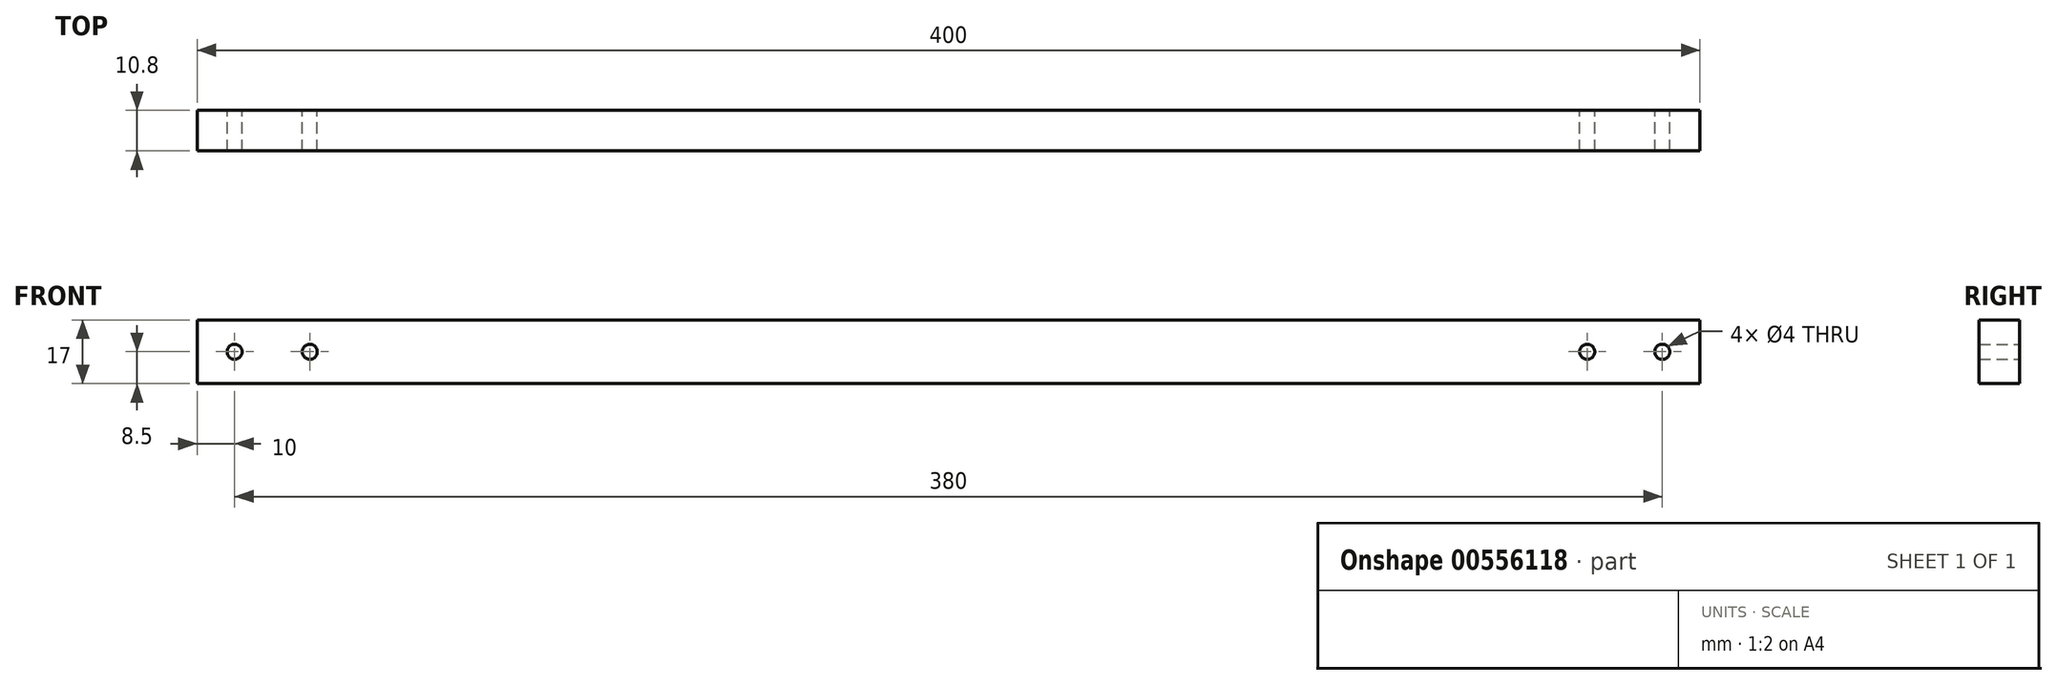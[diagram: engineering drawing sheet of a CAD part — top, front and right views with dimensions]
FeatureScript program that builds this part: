
annotation { "Feature Type Name" : "Feature", "Feature Type Description" : "" }
export const myFeature = defineFeature(function(context is Context, id is Id, definition is map)
    precondition{}
    {
        {
            var Q0;
            Q0=qCreatedBy(makeId("Front.planeOp"),FACE);
            var sketch = newSketch(context, id + "F0", { "sketchPlane" : qUnion([Q0])});
            skLineSegment(sketch, "E0.bottom", {"start": v(200, 8.5) * mm, "end": v(-200, 8.5) * mm});
            skLineSegment(sketch, "E0.top", {"start": v(200, -8.5) * mm, "end": v(-200, -8.5) * mm});
            skLineSegment(sketch, "E0.left", {"start": v(200, 8.5) * mm, "end": v(200, -8.5) * mm});
            skLineSegment(sketch, "E0.right", {"start": v(-200, 8.5) * mm, "end": v(-200, -8.5) * mm});
            skPoint(sketch, "E0.middle", {"position": v(0, 0) * mm});
            skLineSegment(sketch, "E1", {"start": v(-200, 0) * mm, "end": v(200, 0) * mm, "construction": true});
            skPoint(sketch, "E2", {"position": v(-190, 0) * mm});
            skPoint(sketch, "E3", {"position": v(-170, 0) * mm});
            skPoint(sketch, "E4", {"position": v(190, 0) * mm});
            skPoint(sketch, "E5", {"position": v(170, 0) * mm});
            skSolve(sketch);
        }
        {
            var Q0;
            Q0 = qSketchRegion(id + "F0", true);
            extrude(context, id + "F1", {"entities" : qUnion([Q0]), "depth" : 10.8 * mm, "offsetDistance" : 25 * mm});
        }
        {
            var Q0;
            Q0=sQuery(id+"F0.wireOp",VERTEX,"E2");
            var Q1;
            Q1=sQuery(id+"F0.wireOp",VERTEX,"E3");
            var Q2;
            Q2=sQuery(id+"F0.wireOp",VERTEX,"E5");
            var Q3;
            Q3=sQuery(id+"F0.wireOp",VERTEX,"E4");
            var Q4;
            Q4=makeQuery(id+"F1.opExtrude","SWEPT_BODY",BODY,{"disambiguationData":[OSD([sQuery(id+"F0.wireOp",EDGE,"E0.bottom"),sQuery(id+"F0.wireOp",EDGE,"E0.top"),sQuery(id+"F0.wireOp",EDGE,"E0.left"),sQuery(id+"F0.wireOp",EDGE,"E0.right")])]});
            hole(context, id + "F2", {"style" : HoleStyle.SIMPLE, "endStyle" : HoleEndStyle.THROUGH, "oppositeDirection" : true, "holeDiameter" : 4 * mm, "majorDiameter" : 5 * mm, "isTappedThrough" : true, "tappedDepth" : 12 * mm, "tapClearance" : 3, "startFromSketch" : true, "locations" : qUnion([Q0, Q1, Q2, Q3]), "scope" : qUnion([Q4])});
        }
    });
